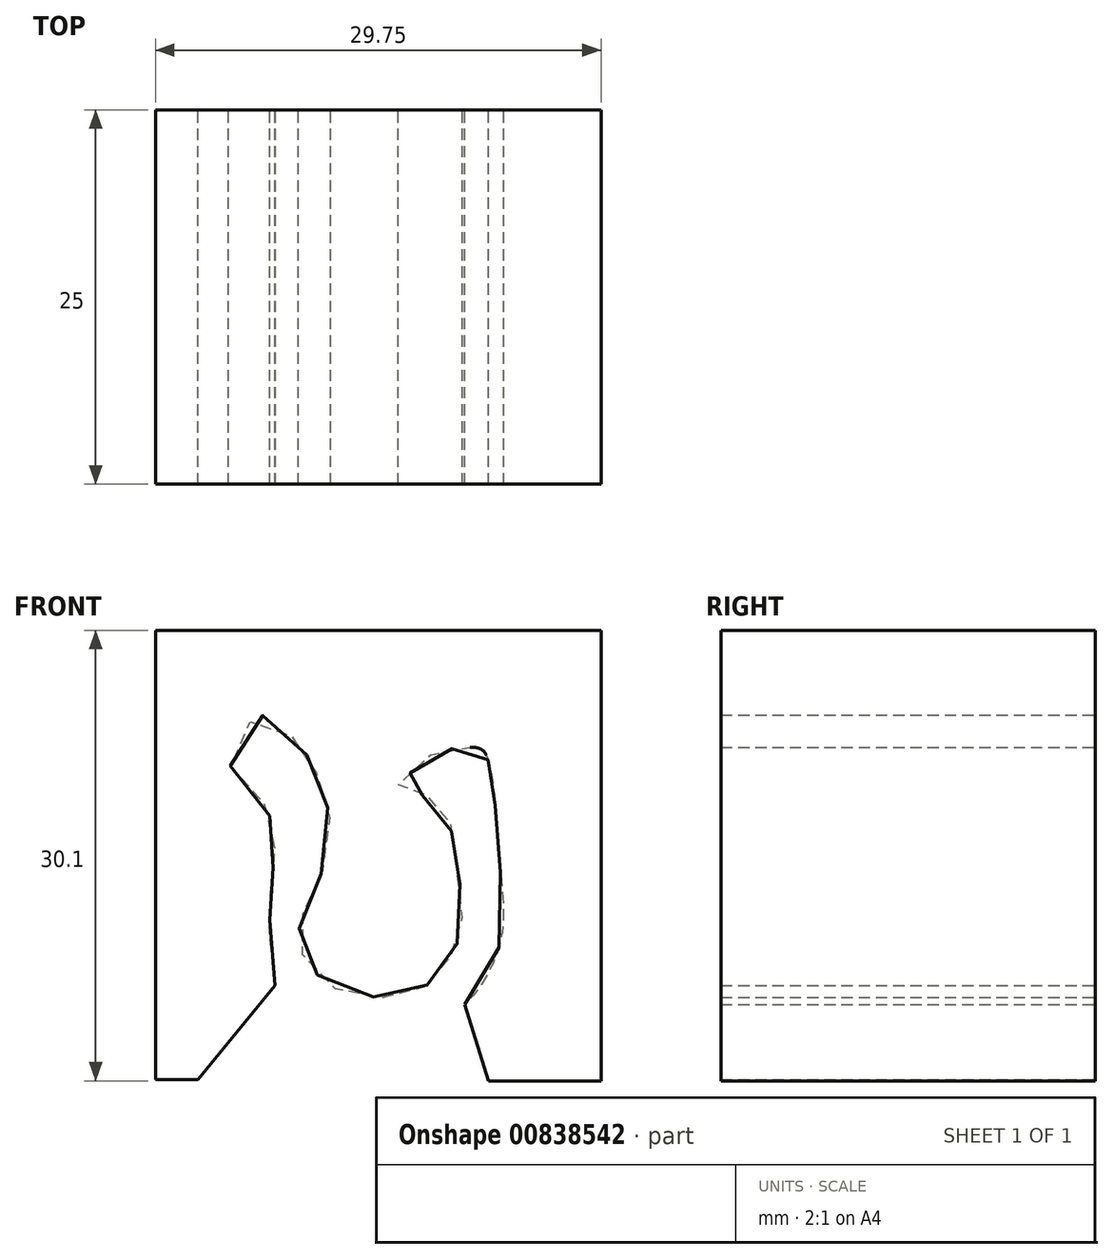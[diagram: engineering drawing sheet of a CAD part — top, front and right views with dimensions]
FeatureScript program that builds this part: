
annotation { "Feature Type Name" : "Feature", "Feature Type Description" : "" }
export const myFeature = defineFeature(function(context is Context, id is Id, definition is map)
    precondition{}
    {
        {
            var Q0;
            Q0=qCreatedBy(makeId("Front.planeOp"),FACE);
            var sketch = newSketch(context, id + "F0", { "sketchPlane" : qUnion([Q0])});
            skFitSpline(sketch, "E0", {"points": [v(-5.29, 6.1) * mm, v(-4.46, 8.22) * mm, v(-2.68, 9.28) * mm, v(-0.96, 7.74) * mm, v(0, 6.5) * mm, v(0.75, 4.91) * mm, v(1.28, 3.25) * mm, v(1.48, 0.93) * mm, v(0.81, -1.43) * mm, v(0, -3.06) * mm, v(-0.6, -4.87) * mm, v(-0.6, -6.13) * mm, v(0, -7.35) * mm, v(1.52, -8.8) * mm, v(3.23, -9.38) * mm, v(5.46, -9.55) * mm, v(7.2, -9.17) * mm, v(8.13, -8.57) * mm, v(9.06, -7.58) * mm, v(9.84, -6.22) * mm, v(10.18, -5.25) * mm, v(10.25, -3.06) * mm, v(9.94, -0.92) * mm, v(9.79, 0) * mm, v(9.52, 2.06) * mm, v(9.12, 3.65) * mm, v(7.77, 3.93) * mm, v(6.62, 4.1) * mm, v(5.99, 4.49) * mm, v(7.02, 5.6) * mm, v(8.12, 6.61) * mm, v(8.67, 6.9) * mm, v(10.53, 7.15) * mm, v(11.51, 7.04) * mm, v(11.84, 6.72) * mm, v(12.04, 6.18) * mm, v(12.27, 5.1) * mm, v(12.43, 3.88) * mm, v(12.53, 2.54) * mm, v(12.66, 0.43) * mm, v(13.04, -3.66) * mm, v(12.78, -6.05) * mm, v(12.08, -7.81) * mm, v(10.45, -10.03) * mm, v(8.6, -10.96) * mm, v(6.07, -11.56) * mm, v(4.17, -11.65) * mm, v(2.2, -11.47) * mm, v(0, -10.62) * mm, v(-0.98, -10) * mm, v(-2.22, -8.74) * mm, v(-2.57, -6.87) * mm, v(-2.56, -4.28) * mm, v(-2.53, -3.4) * mm, v(-2.42, -1.6) * mm, v(-2.23, 0) * mm, v(-2.23, 1.15) * mm, v(-2.76, 3.07) * mm, v(-4.33, 5.18) * mm, v(-5.29, 6.1) * mm]});
            skLineSegment(sketch, "E1.bottom", {"start": v(13.5, 14.97) * mm, "end": v(-10.2, 14.96) * mm});
            skLineSegment(sketch, "E2", {"start": v(-488.36, -15.25) * mm, "end": v(-2417, 11.11) * mm});
            skLineSegment(sketch, "E3", {"start": v(-2417, 11.11) * mm, "end": v(-2417, 47.99) * mm});
            skLineSegment(sketch, "E4", {"start": v(-2.22, -8.74) * mm, "end": v(-7.37, -15.04) * mm});
            skLineSegment(sketch, "E5", {"start": v(-7.37, -15.04) * mm, "end": v(-10.2, -15.04) * mm});
            skLineSegment(sketch, "E6", {"start": v(-10.2, -15.04) * mm, "end": v(-10.2, 14.96) * mm});
            skLineSegment(sketch, "E7", {"start": v(10.45, -10.03) * mm, "end": v(12.04, -15.13) * mm});
            skLineSegment(sketch, "E8", {"start": v(12.04, -15.13) * mm, "end": v(19.56, -15.13) * mm});
            skLineSegment(sketch, "E9", {"start": v(19.56, -15.13) * mm, "end": v(19.55, 14.96) * mm});
            skLineSegment(sketch, "E10", {"start": v(19.55, 14.96) * mm, "end": v(13.5, 14.97) * mm});
            skSolve(sketch);
        }
        {
            var Q0;
            Q0=makeQuery(id+"F0.imprint","IMPRINT",FACE,{"disambiguationData":[TD([[makeQuery(id+"F0.imprint","IMPRINT",EDGE,{"derivedFrom":sQuery(id+"F0.wireOp",EDGE,"E1.bottom")}),1.0]])]});
            extrude(context, id + "F1", {"entities" : qUnion([Q0]), "depth" : 25 * mm, "offsetDistance" : 25 * mm});
        }
    });
